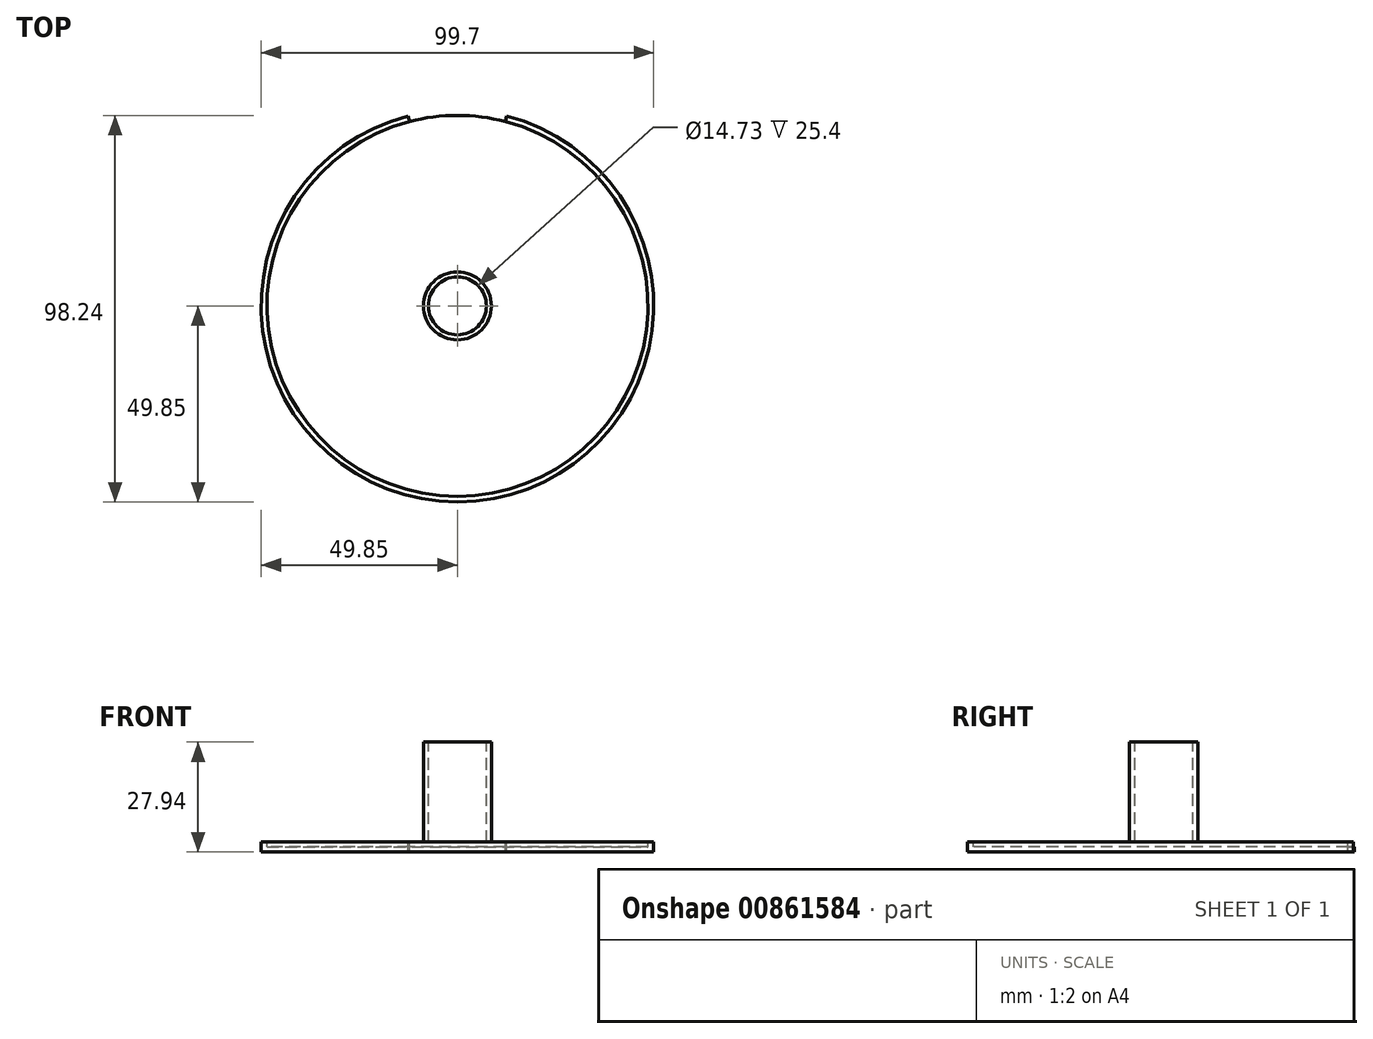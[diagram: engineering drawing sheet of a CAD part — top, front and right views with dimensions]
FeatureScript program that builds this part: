
annotation { "Feature Type Name" : "Feature", "Feature Type Description" : "" }
export const myFeature = defineFeature(function(context is Context, id is Id, definition is map)
    precondition{}
    {
        {
            var Q0;
            Q0=qCreatedBy(makeId("Top.planeOp"),FACE);
            var sketch = newSketch(context, id + "F0", { "sketchPlane" : qUnion([Q0])});
            skCircle(sketch, "E0", {"center": v(0, 0) * mm, "radius": 8.64 * mm});
            skCircle(sketch, "E1", {"center": v(0, 0) * mm, "radius": 7.37 * mm});
            skCircle(sketch, "E2", {"center": v(0, 0) * mm, "radius": 49.85 * mm});
            skSolve(sketch);
        }
        {
            var Q0;
            Q0=makeQuery(id+"F0.imprint","IMPRINT",FACE,{"disambiguationData":[TD([[makeQuery(id+"F0.imprint","IMPRINT",EDGE,{"derivedFrom":sQuery(id+"F0.wireOp",EDGE,"E0")}),1.0]])]});
            var Q1;
            Q1=makeQuery(id+"F0.imprint","IMPRINT",FACE,{"disambiguationData":[TD([[makeQuery(id+"F0.imprint","IMPRINT",EDGE,{"derivedFrom":sQuery(id+"F0.wireOp",EDGE,"5c2379ed-9295-4c80-b16f-b42a5a295724")}),1.0]])]});
            var Q2;
            Q2=makeQuery(id+"F0.imprint","IMPRINT",FACE,{"disambiguationData":[TD([[makeQuery(id+"F0.imprint","IMPRINT",EDGE,{"derivedFrom":sQuery(id+"F0.wireOp",EDGE,"QAO9nzO4-KYBa-wA2r-5TJT-41KAtGvldmcp")}),-1.0]])]});
            extrude(context, id + "F1", {"entities" : qUnion([Q0, Q1, Q2]), "oppositeDirection" : true, "depth" : 25.4 * mm, "offsetDistance" : 25.4 * mm});
        }
        {
            var Q0;
            Q0=makeQuery(id+"F1.opExtrude","CAP_FACE",FACE,{"disambiguationData":[OSD([sQuery(id+"F0.wireOp",EDGE,"E0"),sQuery(id+"F0.wireOp",EDGE,"E1")])],"isStart":false});
            var sketch = newSketch(context, id + "F2", { "sketchPlane" : qUnion([Q0])});
            skCircle(sketch, "E3", {"center": v(0, 0) * mm, "radius": 49.85 * mm});
            skSolve(sketch);
        }
        {
            var Q0;
            Q0=makeQuery(id+"F2.imprint","IMPRINT",FACE,{"disambiguationData":[TD([[makeQuery(id+"F2.imprint","IMPRINT",EDGE,{"derivedFrom":sQuery(id+"F2.wireOp",EDGE,"E3")}),1.0]])]});
            var Q1;
            Q1=makeQuery(id+"F2.imprint","IMPRINT",FACE,{"disambiguationData":[TD([[makeQuery(id+"F2.imprint","IMPRINT",EDGE,{"derivedFrom":makeQuery(id+"F1.opExtrude","CAP_EDGE",EDGE,{"disambiguationData":[OSD([sQuery(id+"F0.wireOp",EDGE,"E1")])],"isStart":false})}),-1.0]])]});
            var Q2;
            Q2=makeQuery(id+"F2.imprint","IMPRINT",FACE,{"disambiguationData":[TD([[makeQuery(id+"F2.imprint","IMPRINT",EDGE,{"derivedFrom":makeQuery(id+"F1.opExtrude","CAP_EDGE",EDGE,{"disambiguationData":[OSD([sQuery(id+"F0.wireOp",EDGE,"E0")])],"isStart":false})}),-1.0]])]});
            extrude(context, id + "F3", {"entities" : qUnion([Q0, Q1, Q2]), "depth" : 2.54 * mm, "offsetDistance" : 25.4 * mm});
        }
        {
            var Q0;
            Q0=makeQuery(id+"F3.opExtrude","CAP_FACE",FACE,{"disambiguationData":[OSD([sQuery(id+"F2.wireOp",EDGE,"E3")])],"isStart":true});
            var sketch = newSketch(context, id + "F4", { "sketchPlane" : qUnion([Q0])});
            skCircle(sketch, "E4", {"center": v(0, 0) * mm, "radius": 48.39 * mm});
            skSolve(sketch);
        }
        {
            var Q0;
            Q0=makeQuery(id+"F4.imprint","IMPRINT",FACE,{"disambiguationData":[TD([[makeQuery(id+"F4.imprint","IMPRINT",EDGE,{"derivedFrom":sQuery(id+"F4.wireOp",EDGE,"E4")}),1.0]])]});
            extrude(context, id + "F5", {"entities" : qUnion([Q0]), "operationType" : NewBodyOperationType.REMOVE, "oppositeDirection" : true, "depth" : 1.27 * mm, "offsetDistance" : 25.4 * mm});
        }
        {
            var Q0;
            Q0=makeQuery(id+"F3.opExtrude","CAP_FACE",FACE,{"disambiguationData":[OSD([sQuery(id+"F2.wireOp",EDGE,"E3")])],"isStart":true});
            var sketch = newSketch(context, id + "F6", { "sketchPlane" : qUnion([Q0])});
            skArc(sketch, "E5", {"start": v(0, 48.39) * mm, "mid": v(-6.15, 48) * mm, "end": v(-12.2, 46.83) * mm});
            skLineSegment(sketch, "E6", {"start": v(-12.2, 46.83) * mm, "end": v(-12.57, 48.24) * mm});
            skArc(sketch, "E7", {"start": v(0, 48.39) * mm, "mid": v(6.15, 48) * mm, "end": v(12.2, 46.83) * mm});
            skLineSegment(sketch, "E8", {"start": v(12.2, 46.83) * mm, "end": v(12.48, 48.26) * mm});
            skArc(sketch, "E9", {"start": v(12.48, 48.26) * mm, "mid": v(-0.04, 49.85) * mm, "end": v(-12.57, 48.24) * mm});
            skSolve(sketch);
        }
        {
            var Q0;
            Q0=makeQuery(id+"F6.imprint","IMPRINT",FACE,{"disambiguationData":[TD([[makeQuery(id+"F6.imprint","IMPRINT",EDGE,{"derivedFrom":sQuery(id+"F6.wireOp",EDGE,"E5")}),-1.0]])]});
            extrude(context, id + "F7", {"entities" : qUnion([Q0]), "operationType" : NewBodyOperationType.REMOVE, "oppositeDirection" : true, "depth" : 25.4 * mm, "offsetDistance" : 25.4 * mm});
        }
    });
